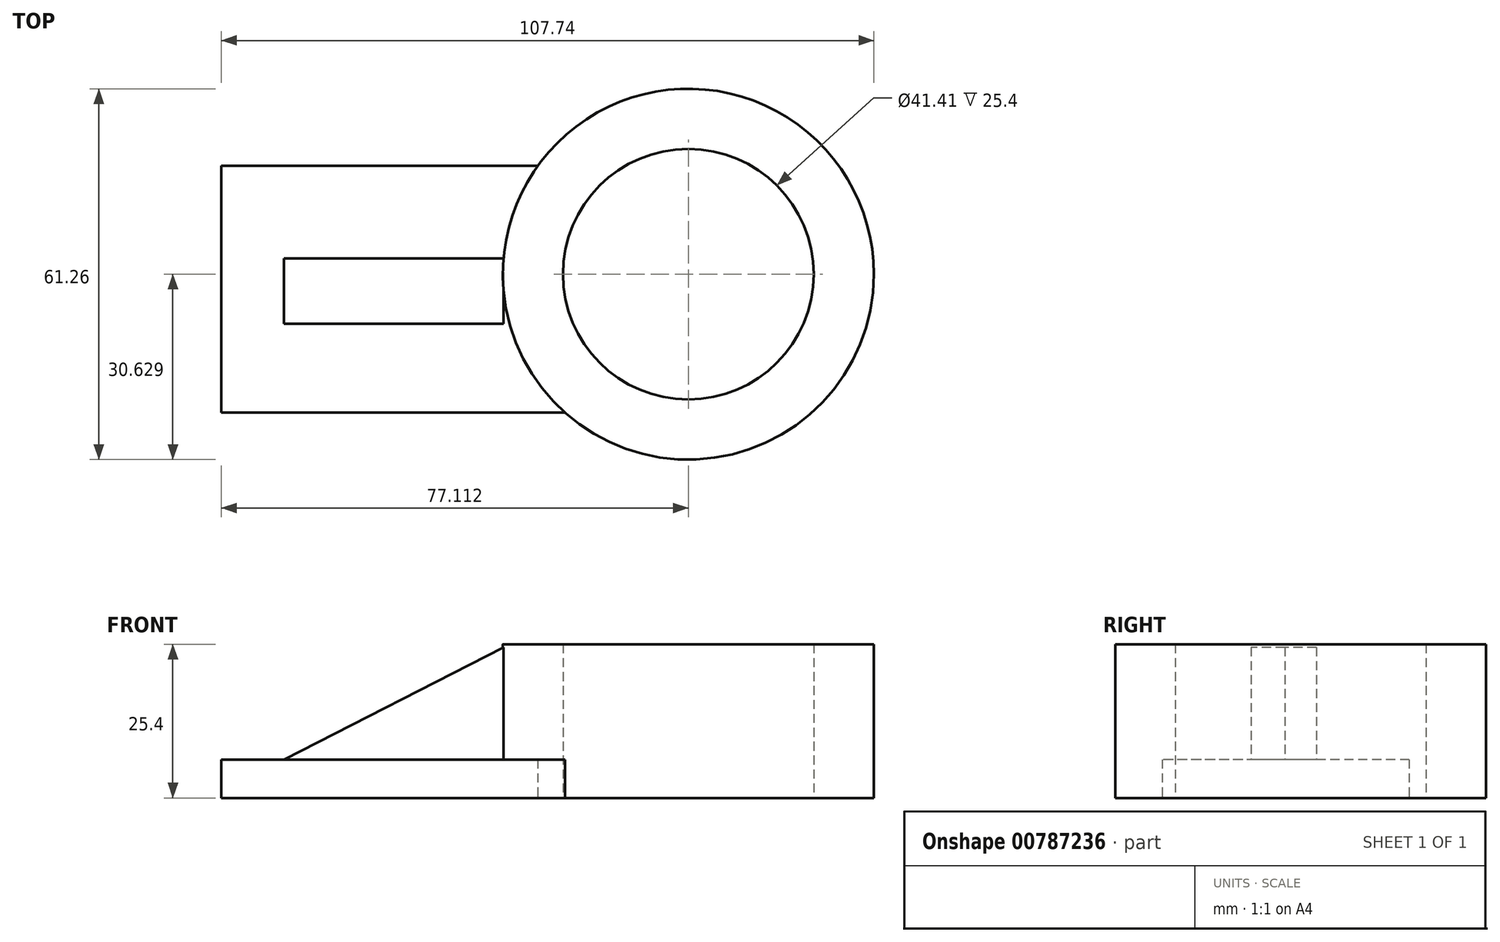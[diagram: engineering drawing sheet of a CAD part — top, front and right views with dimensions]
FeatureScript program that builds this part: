
annotation { "Feature Type Name" : "Feature", "Feature Type Description" : "" }
export const myFeature = defineFeature(function(context is Context, id is Id, definition is map)
    precondition{}
    {
        {
            var Q0;
            Q0=qCreatedBy(makeId("Top.planeOp"),FACE);
            var sketch = newSketch(context, id + "F0", { "sketchPlane" : qUnion([Q0])});
            skCircle(sketch, "E0", {"center": v(44.94, 16.5) * mm, "radius": 30.63 * mm});
            skCircle(sketch, "E1", {"center": v(44.94, 16.5) * mm, "radius": 20.7 * mm});
            skLineSegment(sketch, "E2", {"start": v(20.1, 34.41) * mm, "end": v(-32.17, 34.41) * mm});
            skLineSegment(sketch, "E3", {"start": v(-32.17, -6.39) * mm, "end": v(24.58, -6.39) * mm});
            skLineSegment(sketch, "E4", {"start": v(-32.17, 34.41) * mm, "end": v(-32.17, -6.39) * mm});
            skSolve(sketch);
        }
        {
            var Q0;
            {var subQ0=sQuery(id+"F0.wireOp",EDGE,"E2");Q0=makeQuery(id+"F0.imprint","IMPRINT",FACE,{"disambiguationData":[TD([[makeQuery(id+"F0.imprint","IMPRINT",EDGE,{"derivedFrom":subQ0}),1.0]])]});}
            extrude(context, id + "F1", {"entities" : qUnion([Q0]), "depth" : 6.35 * mm, "offsetDistance" : 25.4 * mm});
        }
        {
            var Q0;
            Q0=makeQuery(id+"F0.imprint","IMPRINT",FACE,{"disambiguationData":[TD([[makeQuery(id+"F0.imprint","IMPRINT",EDGE,{"derivedFrom":sQuery(id+"F0.wireOp",EDGE,"E1")}),-1.0]])]});
            extrude(context, id + "F2", {"entities" : qUnion([Q0]), "operationType" : NewBodyOperationType.ADD, "depth" : 25.4 * mm, "offsetDistance" : 25.4 * mm});
        }
        {
            var Q0;
            Q0=makeQuery(id+"F1.opExtrude","CAP_FACE",FACE,{"disambiguationData":[OSD([sQuery(id+"F0.wireOp",EDGE,"E0"),sQuery(id+"F0.wireOp",EDGE,"E2"),sQuery(id+"F0.wireOp",EDGE,"E3"),sQuery(id+"F0.wireOp",EDGE,"E4")])],"isStart":false});
            var sketch = newSketch(context, id + "F3", { "sketchPlane" : qUnion([Q0])});
            skPoint(sketch, "E5.endSnap0", {"position": v(14.5, 13.15) * mm});
            skLineSegment(sketch, "E6.bottom", {"start": v(14.42, 19.1) * mm, "end": v(-21.81, 19.1) * mm});
            skLineSegment(sketch, "E6.top", {"start": v(14.42, 8.3) * mm, "end": v(-21.81, 8.3) * mm});
            skLineSegment(sketch, "E6.left", {"start": v(14.42, 19.1) * mm, "end": v(14.42, 8.3) * mm});
            skLineSegment(sketch, "E6.right", {"start": v(-21.81, 19.1) * mm, "end": v(-21.81, 8.3) * mm});
            skSolve(sketch);
        }
        {
            var Q0;
            {var subQ4=sQuery(id+"F3.wireOp",EDGE,"E6.bottom");Q0=makeQuery(id+"F3.imprint","IMPRINT",FACE,{"disambiguationData":[TD([[makeQuery(id+"F3.imprint","IMPRINT",EDGE,{"derivedFrom":subQ4}),1.0]])]});}
            extrude(context, id + "F4", {"entities" : qUnion([Q0]), "operationType" : NewBodyOperationType.ADD, "depth" : 18.54 * mm, "offsetDistance" : 25.4 * mm});
        }
        {
            var Q0;
            Q0=makeQuery(id+"F4.opExtrude","SWEPT_FACE",FACE,{"disambiguationData":[OSD([sQuery(id+"F3.wireOp",EDGE,"E6.top")])]});
            var sketch = newSketch(context, id + "F5", { "sketchPlane" : qUnion([Q0])});
            skLineSegment(sketch, "E7", {"start": v(-21.81, 6.35) * mm, "end": v(14.42, 24.9) * mm});
            skSolve(sketch);
        }
        {
            var Q0;
            Q0=makeQuery(id+"F5.imprint","IMPRINT",FACE,{"disambiguationData":[TD([[makeQuery(id+"F5.imprint","IMPRINT",EDGE,{"derivedFrom":sQuery(id+"F5.wireOp",EDGE,"E7")}),1.0]])]});
            extrude(context, id + "F6", {"entities" : qUnion([Q0]), "operationType" : NewBodyOperationType.REMOVE, "oppositeDirection" : true, "depth" : 25.4 * mm, "offsetDistance" : 25.4 * mm});
        }
    });
